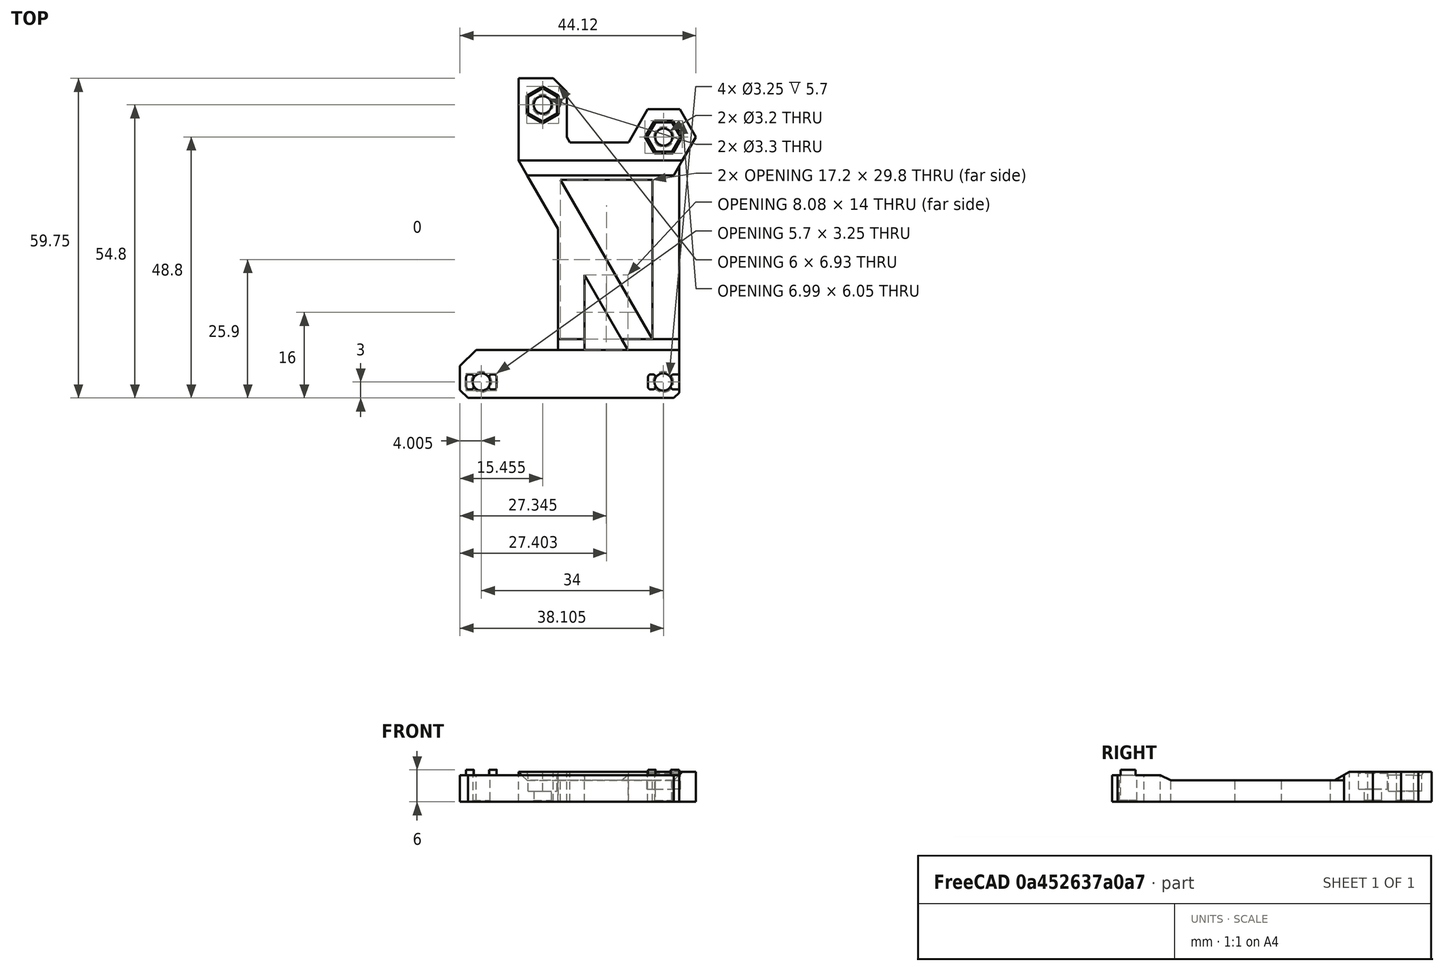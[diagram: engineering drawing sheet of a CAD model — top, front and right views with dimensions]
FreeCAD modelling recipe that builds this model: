
FCSTD DOCUMENT  (FreeCAD 0.18R16146 (Git))
Label: hemera-5015-fan-adapter
License: All rights reserved
LicenseURL: http://en.wikipedia.org/wiki/All_rights_reserved
objects: Part::Box×4, Part::Cut×3, Part::Feature×2, Part::Chamfer×2, Mesh::Feature×2, Part::MultiFuse×1
note: 12 computed .brp shape members not serialized (recipe doc carries the construction recipe); baked Part::Feature solids carry a one-line shape summary decoded from their .brp

FEATURE [Part::Feature] Part__Feature023  label="body_front"
  Placement = pos=(-35.975,23,59) rot=(0.57735,0.57735,-0.57735;2.0944rad)
  shape: bbox 44.13 x 79.97 x 28.92 mm, 174 faces (baked)
FEATURE [Part::Box] Box  label="Cube"
  AttacherType = Attacher::AttachEngine3D
  Height = 33
  Length = 70
  Placement = pos=(-33,-43.2,0) rot=(0,0,1;0rad)
  Width = 26
FEATURE [Part::Cut] Cut
  Base = -> Part__Feature023
  Tool = -> Box
FEATURE [Part::Chamfer] Chamfer
  Base = -> Cut
  Edges = 1 edges r=1.5: [Edge22]
FEATURE [Part::Box] Box001  label="Cube001"
  AttacherType = Attacher::AttachEngine3D
  Height = 13
  Length = 10
  Placement = pos=(20.52,-22.8,0) rot=(0,0,1;0rad)
  Width = 49
FEATURE [Part::Box] Box002  label="Cube002"
  AttacherType = Attacher::AttachEngine3D
  Height = 10
  Length = 20
  Placement = pos=(-8,-20,5) rot=(0,0,1;0rad)
  Width = 10
FEATURE [Part::Box] Box003  label="Cube003"
  AttacherType = Attacher::AttachEngine3D
  Height = 2
  Length = 2
  Placement = pos=(18.52,-7,0) rot=(0,0,1;0rad)
  Width = 34
FEATURE [Part::MultiFuse] Fusion
  Shapes = -> [Box003,Chamfer]
FEATURE [Part::Cut] Cut001
  Base = -> Fusion
  Tool = -> Box002
FEATURE [Part::Cut] Cut002
  Base = -> Cut001
  Tool = -> Box001
FEATURE [Part::Chamfer] Chamfer001
  Base = -> Cut002
  Edges = 1 edges r=1: [Edge39]
FEATURE [Part::Feature] Chamfer001001  label="Chamfer002"
  shape: bbox 44.12 x 59.75 x 6 mm, 100 faces (baked)
FEATURE [Mesh::Feature] nozzle_fan_duct
FEATURE [Mesh::Feature] nozzle_fan_spacer
